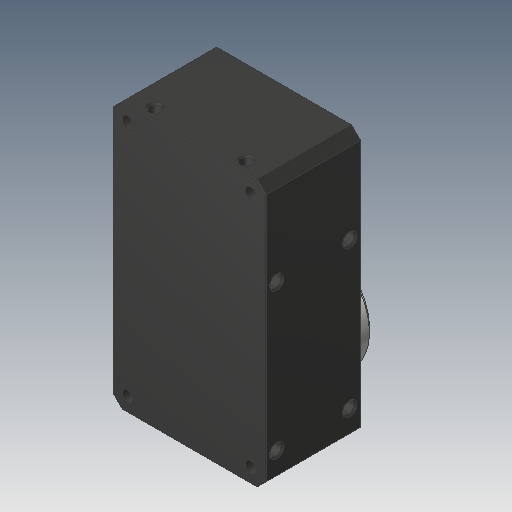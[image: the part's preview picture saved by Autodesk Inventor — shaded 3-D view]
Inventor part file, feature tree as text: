
AUTODESK INVENTOR PART (.ipt)
format: ipt  version: 2019.4 (Build 234330000, 330)  size: 369,664 bytes
history: native  units: mm
features: sketch x8, extrude x7, chamfer x3, other x1, mirror x1
ambient origin geometry x8: Origin, YZ Plane, XZ Plane, XY Plane, X Axis, Y Axis, Z Axis, Center Point
bodies: Body1 (feature_tree)
feature tree (20):
  other  "ソリッド1"
  extrude  "押し出し1"  Depth=2.0mm
  extrude  "押し出し5"  Depth=2.0mm
  extrude  "押し出し6"  Depth=2.0mm
  mirror  "ミラー1"
  extrude  "押し出し7"  Depth=2.0mm
  extrude  "押し出し8"  Depth=2.0mm
  chamfer  "面取り3"  Distance=2.0mm
  extrude  "押し出し9"  Depth=2.0mm
  extrude  "押し出し10"  Depth=2.0mm
  chamfer  "面取り4"  Distance=33.5mm
  chamfer  "面取り5"  Distance=26.0mm
  sketch  "スケッチ1"
  sketch  "スケッチ6"
  sketch  "スケッチ7"
  sketch  "スケッチ8"
  sketch  "スケッチ9"
  sketch  "スケッチ10"
  sketch  "スケッチ11"
  sketch  "スケッチ12"
